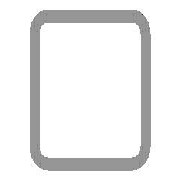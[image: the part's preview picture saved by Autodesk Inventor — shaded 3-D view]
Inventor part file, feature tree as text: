
AUTODESK INVENTOR PART (.ipt)
format: ipt  version: 2025 (Build 290162010, 162A)  size: 134,656 bytes
history: native  units: mm (DEFAULTED — no unit token found)
features: other x4, sketch x1, plane x1
ambient origin geometry x8: Origin, YZ Plane, XZ Plane, XY Plane, X Axis, Y Axis, Z Axis, Center Point
bodies: Solid1 (feature_tree), Body (feature_tree)
feature tree (6):
  parser-record x1  (decoder bookkeeping rows leaked as tree rows — omitted from the tree; the rows remain in map.json)
  other  "Driven Length"
  other  "Start Plane"
  other  "End Plane"
  sketch  "Sketch3"  dims[d3=898.0mm d4=0.0mm d7=4.0mm d9=40.0mm d11=40.0mm d12=2.0mm d13=-0.0mm d14=898.0mm d15=20.0mm d16=20.0mm d17=90.0deg d18=898.0mm]
  plane  "Work Plane3"
